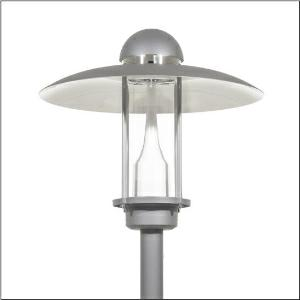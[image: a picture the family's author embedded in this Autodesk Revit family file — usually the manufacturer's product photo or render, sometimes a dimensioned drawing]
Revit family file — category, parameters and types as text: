
# Revit family: city-light_elegance_iq___pl1_2s_5xa5265jf14h000022_4ac6
name_source: partatom
category: Lighting Fixtures
units: mm (PartAtom-declared; Revit-internal decimal feet)

## family parameters
Cut with Voids When Loaded = No
Host = Face
Light Source = No
Part Type = Normal
Room Calculation Point = No
Round Connector Dimension = Use Diameter
Shared = No

## types (1)
- --- (1 x LED, 2840 lm, 19.3 W, 3000K)
    Apparent Load = 19 VA
    CIE Flux Codes = 24 63 94 98 100
    Color Rendering = 70
    Color Temperature = 3000K
    Default Elevation = 1800 mm
    Description = City-Light Elegance iQ, mast luminaire, Module 540 iQ-SR, primary light control with 3 zone facetted reflector, of plastic, silver coated, highly specular, structured, primary optical cover: cover, of PMMA, transparent, light distribution: PL1.2s, light emission: direct distribution, primary light characteristic: symmetric, installation type: post-top, LED, High Power LED, rated luminous flux: 2.840lm, luminous efficacy: 147lm/W, light colour: 730, colour temperature: 3000K, control gear: ECG iQ, control: Street-Remote, Auto-Match, Temp-Guard, Lumen-Switch, Night-Set, Smart-Wire, Light-Fading, Desk-Remote (wireless, voltage-free reading and setting of iQ features in the workshop via application-optimized NFC function/RFID function), optimised constant luminous flux control (CLO 2.0), presetting dimming logarithmic, mains connection: 230..240V, AC, 50/60Hz, connection cable pre-assembled, cable length: 5,5m, wiring characteristics: H07RN-F, start of lifetime: 19W, end of service life: 21W, reduction: 10W, luminaire housing, upper part, of aluminium, coated, Siteco® metallic grey (DB 702S), diameter: 750mm, height: 675mm, spigot size: d x l = 76 x 70mm (post-top) | with reducer (optional accessory) 60 x 70mm, post-top mast mounting element, of diecast aluminium, coated, Siteco® metallic grey (DB 702S), Module 540 iQ-SR, traffic white (RAL 9016), equipment: standard, protection rating (complete): IP65, insulation class (complete): insulation class II (safety insulation), certification: CE, ENEC, VDE, packaging unit: 1 piece

Light Distribution: PL1.2s
    Height = 675 mm
    Lamp = 1 x LED
    Lamp Light Flux = 2840 lm
    Lamp Power = 19.3 W
    Lamp count = 1
    Length = 750 mm
    Luminous efficacy = 147 lm/W
    Manufacturer = Siteco
    ModVariant = No
    Model = 5XA5265JF14H000022
    Number of Poles = 1
    OnlyDefault = Yes
    Power Factor = 1
    Product Name = City-Light Elegance iQ | PL1.2s
    Product group = mast luminaire | pylon top
    ProductGroupID = 6100
    Protection Class = Protection class II
    Protection Degree = IP 65
    RLX_Detail_Level = 1
    RLX_Emergency_Light_Flux = 0 lm
    RLX_Emergency_Type = 0
    RLX_Emergency_Type_DB = No
    RlxData = <blob elided: 72533 chars, md5=81da67aa>
    Socket = socket
    Standby Power = 0 W
    System Light Flux = 2840 lm
    System Power = 19 W
    Type Comments = factory setting: luminous flux: 100 % | dim-lin: 254 | 403 mA
    Type Image = l_1006912.jpg
    URL = http://relux.com
    VarID = @adj_094871
    Voltage = 0 V
    Weight = 0.00 kg
    Width = 0 mm  [stored 0 ft]

note: [stored X ft] marks values corroborated as IEEE doubles in the binary element streams (Revit-internal decimal feet)

## geometry (parser evidence)
native form markers: Blend x4, Sweep x8
no freeform markers — native parametric forms only
